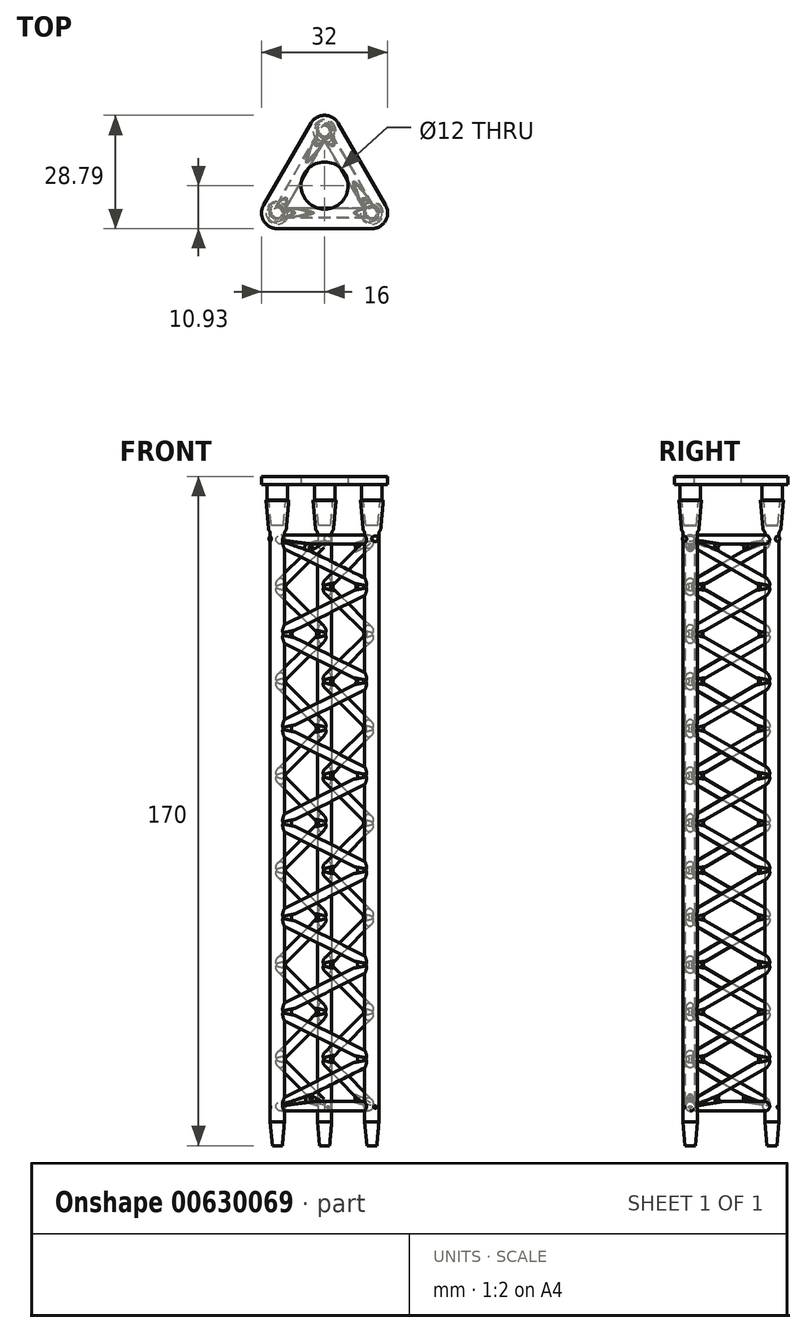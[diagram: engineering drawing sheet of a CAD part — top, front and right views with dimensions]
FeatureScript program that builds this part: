
annotation { "Feature Type Name" : "Feature", "Feature Type Description" : "" }
export const myFeature = defineFeature(function(context is Context, id is Id, definition is map)
    precondition{}
    {
        {
            var Q0;
            Q0=qCreatedBy(makeId("Top.planeOp"),FACE);
            var sketch = newSketch(context, id + "F0", { "sketchPlane" : qUnion([Q0])});
            skLineSegment(sketch, "E0", {"start": v(-12, -6.93) * mm, "end": v(12, -6.93) * mm});
            skLineSegment(sketch, "E1", {"start": v(12, -6.93) * mm, "end": v(0, 13.86) * mm});
            skLineSegment(sketch, "E2", {"start": v(0, 13.86) * mm, "end": v(-12, -6.93) * mm});
            skLineSegment(sketch, "E3", {"start": v(-6, 3.46) * mm, "end": v(12, -6.93) * mm});
            skLineSegment(sketch, "E4", {"start": v(6, 3.46) * mm, "end": v(-12, -6.93) * mm});
            skLineSegment(sketch, "E5", {"start": v(0, 13.86) * mm, "end": v(0, -6.93) * mm});
            skSolve(sketch);
        }
        {
            var Q0;
            Q0=qCreatedBy(makeId("Front.planeOp"),FACE);
            var sketch = newSketch(context, id + "F1", { "sketchPlane" : qUnion([Q0])});
            skLineSegment(sketch, "E6", {"start": v(0, 0) * mm, "end": v(0, 15.44) * mm});
            skSolve(sketch);
        }
        {
            var Q0;
            Q0=qCreatedBy(makeId("Top.planeOp"),FACE);
            var sketch = newSketch(context, id + "F2", { "sketchPlane" : qUnion([Q0])});
            skCircle(sketch, "E7", {"center": v(-12, -6.93) * mm, "radius": 1.8 * mm});
            skSolve(sketch);
        }
        {
            var Q0;
            Q0=makeQuery(id+"F2.imprint","IMPRINT",FACE,{"disambiguationData":[TD([[makeQuery(id+"F2.imprint","IMPRINT",EDGE,{"derivedFrom":sQuery(id+"F2.wireOp",EDGE,"E7")}),1.0]])]});
            var Q1;
            Q1=sQuery(id+"F2.wireOp",EDGE,"E7");
            extrude(context, id + "F3", {"entities" : qUnion([Q0]), "surfaceEntities" : qUnion([Q1]), "depth" : 154 * mm, "offsetDistance" : 25 * mm, "hasSecondDirection" : true, "secondDirectionOppositeDirection" : true, "secondDirectionDepth" : 10 * mm});
        }
        {
            var Q0;
            Q0=qCreatedBy(makeId("Right.planeOp"),FACE);
            var sketch = newSketch(context, id + "F4", { "sketchPlane" : qUnion([Q0])});
            skCircle(sketch, "E8", {"center": v(-6.93, 0) * mm, "radius": 1.2 * mm});
            skSolve(sketch);
        }
        {
            var Q0;
            Q0=sQuery(id+"F0.wireOp",EDGE,"E0");
            var Q1;
            Q1=sQuery(id+"F1.wireOp",EDGE,"E6");
            cPlane(context, id + "F5", {"entities" : qUnion([Q0, Q1]), "cplaneType" : CPlaneType.LINE_ANGLE, "offset" : 25 * mm, "angle" : 0 * degree, "width" : 150 * mm, "height" : 150 * mm});
        }
        {
            var Q0;
            Q0=qCreatedBy(id+"F5.planeOp",FACE);
            var sketch = newSketch(context, id + "F6", { "sketchPlane" : qUnion([Q0])});
            skLineSegment(sketch, "E9", {"start": v(-12, 0) * mm, "end": v(12, 12) * mm});
            skLineSegment(sketch, "E10", {"start": v(12, 12) * mm, "end": v(12, 0) * mm, "construction": true});
            skLineSegment(sketch, "E11", {"start": v(-12, 0) * mm, "end": v(-12, 24) * mm, "construction": true});
            skLineSegment(sketch, "E12", {"start": v(-12, 24) * mm, "end": v(12, 12) * mm});
            skLineSegment(sketch, "E13", {"start": v(-12, 24) * mm, "end": v(12, 36) * mm});
            skLineSegment(sketch, "E14", {"start": v(12, 36) * mm, "end": v(-12, 48) * mm});
            skLineSegment(sketch, "E15", {"start": v(-12, 48) * mm, "end": v(12, 60) * mm});
            skLineSegment(sketch, "E16", {"start": v(12, 60) * mm, "end": v(-12, 72) * mm});
            skLineSegment(sketch, "E17", {"start": v(-12, 72) * mm, "end": v(12, 84) * mm});
            skLineSegment(sketch, "E18", {"start": v(12, 84) * mm, "end": v(-12, 96) * mm});
            skLineSegment(sketch, "E19", {"start": v(-12, 96) * mm, "end": v(-12, 72) * mm, "construction": true});
            skLineSegment(sketch, "E20", {"start": v(-12, 48) * mm, "end": v(-12, 24) * mm, "construction": true});
            skLineSegment(sketch, "E21", {"start": v(-12, 48) * mm, "end": v(-12, 72) * mm, "construction": true});
            skLineSegment(sketch, "E22", {"start": v(12, 12) * mm, "end": v(12, 36) * mm, "construction": true});
            skLineSegment(sketch, "E23", {"start": v(12, 36) * mm, "end": v(12, 60) * mm, "construction": true});
            skLineSegment(sketch, "E24", {"start": v(12, 60) * mm, "end": v(12, 84) * mm, "construction": true});
            skLineSegment(sketch, "E25", {"start": v(-12, 96) * mm, "end": v(12, 108) * mm});
            skLineSegment(sketch, "E26", {"start": v(12, 108) * mm, "end": v(12, 84) * mm, "construction": true});
            skLineSegment(sketch, "E27", {"start": v(-12.25, 120) * mm, "end": v(12, 108) * mm});
            skLineSegment(sketch, "E28", {"start": v(-12.25, 120) * mm, "end": v(-12, 96) * mm, "construction": true});
            skLineSegment(sketch, "E29", {"start": v(12, 0) * mm, "end": v(-12, 0) * mm});
            skLineSegment(sketch, "E30", {"start": v(12, 108) * mm, "end": v(12, 132) * mm, "construction": true});
            skLineSegment(sketch, "E31", {"start": v(12, 132) * mm, "end": v(-12.25, 120) * mm});
            skLineSegment(sketch, "E32", {"start": v(-12.25, 120) * mm, "end": v(-12.25, 144) * mm, "construction": true});
            skLineSegment(sketch, "E33", {"start": v(12, 132) * mm, "end": v(-12.25, 144) * mm});
            skLineSegment(sketch, "E34", {"start": v(12, 144) * mm, "end": v(-12.25, 144) * mm});
            skLineSegment(sketch, "E35", {"start": v(12, 132) * mm, "end": v(12, 144) * mm, "construction": true});
            skSolve(sketch);
        }
        {
            var Q0;
            Q0=sQuery(id+"F0.wireOp",VERTEX,"E4.end");
            var Q1;
            Q1=sQuery(id+"F6.wireOp",EDGE,"E9");
            cPlane(context, id + "F7", {"entities" : qUnion([Q0, Q1]), "cplaneType" : CPlaneType.LINE_POINT, "offset" : 25 * mm, "width" : 150 * mm, "height" : 150 * mm});
        }
        {
            var Q0;
            Q0=qCreatedBy(id+"F7.planeOp",FACE);
            var sketch = newSketch(context, id + "F8", { "sketchPlane" : qUnion([Q0])});
            skCircle(sketch, "E36", {"center": v(-6.93, 5.37) * mm, "radius": 1.2 * mm});
            skSolve(sketch);
        }
        {
            var Q0;
            Q0=makeQuery(id+"F8.imprint","IMPRINT",FACE,{"disambiguationData":[TD([[makeQuery(id+"F8.imprint","IMPRINT",EDGE,{"derivedFrom":sQuery(id+"F8.wireOp",EDGE,"E36")}),1.0]])]});
            var Q1;
            Q1=sQuery(id+"F6.wireOp",EDGE,"E9");
            var Q2;
            Q2=sQuery(id+"F6.wireOp",EDGE,"E12");
            var Q3;
            Q3=sQuery(id+"F6.wireOp",EDGE,"E13");
            var Q4;
            Q4=sQuery(id+"F6.wireOp",EDGE,"E14");
            var Q5;
            Q5=sQuery(id+"F6.wireOp",EDGE,"E15");
            var Q6;
            Q6=sQuery(id+"F6.wireOp",EDGE,"E16");
            var Q7;
            Q7=sQuery(id+"F6.wireOp",EDGE,"E17");
            var Q8;
            Q8=sQuery(id+"F6.wireOp",EDGE,"E18");
            var Q9;
            Q9=sQuery(id+"F6.wireOp",EDGE,"E25");
            var Q10;
            Q10=sQuery(id+"F6.wireOp",EDGE,"E27");
            var Q11;
            Q11=sQuery(id+"F6.wireOp",EDGE,"E29");
            var Q12;
            Q12=sQuery(id+"F6.wireOp",EDGE,"E31");
            var Q13;
            Q13=sQuery(id+"F6.wireOp",EDGE,"E33");
            var Q14;
            Q14=sQuery(id+"F6.wireOp",EDGE,"E34");
            sweep(context, id + "F9", {"profiles" : qUnion([Q0]), "path" : qUnion([Q1, Q2, Q3, Q4, Q5, Q6, Q7, Q8, Q9, Q10, Q11, Q12, Q13, Q14])});
        }
        {
            var Q0;
            Q0=makeQuery(id+"F9.opSweep","MID_CAP_EDGE",EDGE,{"disambiguationData":[OSD([sQuery(id+"F6.wireOp",VERTEX,"E33.start"),sQuery(id+"F8.wireOp",EDGE,"E36")])],"capPos":12.0});
            var Q1;
            Q1=makeQuery(id+"F9.opSweep","MID_CAP_EDGE",EDGE,{"disambiguationData":[OSD([sQuery(id+"F6.wireOp",VERTEX,"E34.end"),sQuery(id+"F8.wireOp",EDGE,"E36")])],"capPos":13.0});
            var Q2;
            Q2=makeQuery(id+"F9.opSweep","MID_CAP_EDGE",EDGE,{"disambiguationData":[OSD([sQuery(id+"F6.wireOp",VERTEX,"E31.end"),sQuery(id+"F8.wireOp",EDGE,"E36")])],"capPos":11.0});
            var Q3;
            Q3=makeQuery(id+"F9.opSweep","MID_CAP_EDGE",EDGE,{"disambiguationData":[OSD([sQuery(id+"F6.wireOp",VERTEX,"E27.end"),sQuery(id+"F8.wireOp",EDGE,"E36")])],"capPos":10.0});
            var Q4;
            Q4=makeQuery(id+"F9.opSweep","MID_CAP_EDGE",EDGE,{"disambiguationData":[OSD([sQuery(id+"F6.wireOp",VERTEX,"E25.start"),sQuery(id+"F8.wireOp",EDGE,"E36")])],"capPos":9.0});
            var Q5;
            Q5=makeQuery(id+"F9.opSweep","MID_CAP_EDGE",EDGE,{"disambiguationData":[OSD([sQuery(id+"F6.wireOp",VERTEX,"E18.start"),sQuery(id+"F8.wireOp",EDGE,"E36")])],"capPos":8.0});
            var Q6;
            Q6=makeQuery(id+"F9.opSweep","MID_CAP_EDGE",EDGE,{"disambiguationData":[OSD([sQuery(id+"F6.wireOp",VERTEX,"E17.start"),sQuery(id+"F8.wireOp",EDGE,"E36")])],"capPos":7.0});
            var Q7;
            Q7=makeQuery(id+"F9.opSweep","MID_CAP_EDGE",EDGE,{"disambiguationData":[OSD([sQuery(id+"F6.wireOp",VERTEX,"E16.start"),sQuery(id+"F8.wireOp",EDGE,"E36")])],"capPos":6.0});
            var Q8;
            Q8=makeQuery(id+"F9.opSweep","MID_CAP_EDGE",EDGE,{"disambiguationData":[OSD([sQuery(id+"F6.wireOp",VERTEX,"E15.start"),sQuery(id+"F8.wireOp",EDGE,"E36")])],"capPos":5.0});
            var Q9;
            Q9=makeQuery(id+"F9.opSweep","MID_CAP_EDGE",EDGE,{"disambiguationData":[OSD([sQuery(id+"F6.wireOp",VERTEX,"E14.start"),sQuery(id+"F8.wireOp",EDGE,"E36")])],"capPos":4.0});
            var Q10;
            Q10=makeQuery(id+"F9.opSweep","MID_CAP_EDGE",EDGE,{"disambiguationData":[OSD([sQuery(id+"F6.wireOp",VERTEX,"E13.start"),sQuery(id+"F8.wireOp",EDGE,"E36")])],"capPos":3.0});
            var Q11;
            Q11=makeQuery(id+"F9.opSweep","MID_CAP_EDGE",EDGE,{"disambiguationData":[OSD([sQuery(id+"F6.wireOp",VERTEX,"E12.end"),sQuery(id+"F8.wireOp",EDGE,"E36")])],"capPos":2.0});
            var Q12;
            Q12=makeQuery(id+"F9.opSweep","MID_CAP_EDGE",EDGE,{"disambiguationData":[OSD([sQuery(id+"F6.wireOp",VERTEX,"E29.end"),sQuery(id+"F8.wireOp",EDGE,"E36")])],"capPos":1.0});
            fillet(context, id + "F10", {"entities" : qUnion([Q0, Q1, Q2, Q3, Q4, Q5, Q6, Q7, Q8, Q9, Q10, Q11, Q12]), "radius" : 1 * mm, "tangentPropagation" : true, "defaultsChanged" : false, "vertexSettings" : [], "allowEdgeOverflow" : false});
        }
        {
            var Q0;
            Q0=makeQuery(id+"FOFZZQhrRr9CB2q_1.opPattern","COPY",BODY,{"derivedFrom":makeQuery(id+"FBj1d7q4FQKIzEE_0.opExtrude","SWEPT_BODY",BODY,{"disambiguationData":[OSD([sQuery(id+"F4.wireOp",EDGE,"E8")])]}),"instanceName":"1"});
            var Q1;
            Q1=makeQuery(id+"FBj1d7q4FQKIzEE_0.opExtrude","SWEPT_BODY",BODY,{"disambiguationData":[OSD([sQuery(id+"F4.wireOp",EDGE,"E8")])]});
            var Q2;
            Q2=makeQuery(id+"F3.opExtrude","SWEPT_BODY",BODY,{"disambiguationData":[OSD([sQuery(id+"F2.wireOp",EDGE,"E7")])]});
            var Q3;
            Q3=makeQuery(id+"F9.opSweep","SWEPT_BODY",BODY,{"disambiguationData":[OSD([sQuery(id+"F6.wireOp",EDGE,"E27"),sQuery(id+"F8.wireOp",EDGE,"E36")])]});
            var Q4;
            Q4=sQuery(id+"F1.wireOp",EDGE,"E6");
            circularPattern(context, id + "F11", {"entities" : qUnion([Q0, Q1, Q2, Q3]), "axis" : qUnion([Q4]), "angle" : 360 * degree, "instanceCount" : 3, "equalSpace" : true});
        }
        {
            var Q0;
            Q0=makeQuery(id+"F9.opSweep","SWEPT_BODY",BODY,{"disambiguationData":[OSD([sQuery(id+"F6.wireOp",EDGE,"E27"),sQuery(id+"F8.wireOp",EDGE,"E36")])]});
            var Q1;
            Q1=makeQuery(id+"F11.opPattern","COPY",BODY,{"derivedFrom":makeQuery(id+"F9.opSweep","SWEPT_BODY",BODY,{"disambiguationData":[OSD([sQuery(id+"F6.wireOp",EDGE,"E27"),sQuery(id+"F8.wireOp",EDGE,"E36")])]}),"instanceName":"1"});
            var Q2;
            Q2=makeQuery(id+"F11.opPattern","COPY",BODY,{"derivedFrom":makeQuery(id+"F9.opSweep","SWEPT_BODY",BODY,{"disambiguationData":[OSD([sQuery(id+"F6.wireOp",EDGE,"E27"),sQuery(id+"F8.wireOp",EDGE,"E36")])]}),"instanceName":"2"});
            var Q3;
            Q3=makeQuery(id+"F11.opPattern","COPY",BODY,{"derivedFrom":makeQuery(id+"FOFZZQhrRr9CB2q_1.opPattern","COPY",BODY,{"derivedFrom":makeQuery(id+"FBj1d7q4FQKIzEE_0.opExtrude","SWEPT_BODY",BODY,{"disambiguationData":[OSD([sQuery(id+"F4.wireOp",EDGE,"E8")])]}),"instanceName":"1"}),"instanceName":"2"});
            var Q4;
            Q4=makeQuery(id+"F3.opExtrude","SWEPT_BODY",BODY,{"disambiguationData":[OSD([sQuery(id+"F2.wireOp",EDGE,"E7")])]});
            var Q5;
            Q5=makeQuery(id+"FBj1d7q4FQKIzEE_0.opExtrude","SWEPT_BODY",BODY,{"disambiguationData":[OSD([sQuery(id+"F4.wireOp",EDGE,"E8")])]});
            var Q6;
            Q6=makeQuery(id+"F11.opPattern","COPY",BODY,{"derivedFrom":makeQuery(id+"F3.opExtrude","SWEPT_BODY",BODY,{"disambiguationData":[OSD([sQuery(id+"F2.wireOp",EDGE,"E7")])]}),"instanceName":"1"});
            var Q7;
            Q7=makeQuery(id+"F11.opPattern","COPY",BODY,{"derivedFrom":makeQuery(id+"F3.opExtrude","SWEPT_BODY",BODY,{"disambiguationData":[OSD([sQuery(id+"F2.wireOp",EDGE,"E7")])]}),"instanceName":"2"});
            var Q8;
            Q8=makeQuery(id+"F11.opPattern","COPY",BODY,{"derivedFrom":makeQuery(id+"FBj1d7q4FQKIzEE_0.opExtrude","SWEPT_BODY",BODY,{"disambiguationData":[OSD([sQuery(id+"F4.wireOp",EDGE,"E8")])]}),"instanceName":"2"});
            var Q9;
            Q9=makeQuery(id+"F11.opPattern","COPY",BODY,{"derivedFrom":makeQuery(id+"FOFZZQhrRr9CB2q_1.opPattern","COPY",BODY,{"derivedFrom":makeQuery(id+"FBj1d7q4FQKIzEE_0.opExtrude","SWEPT_BODY",BODY,{"disambiguationData":[OSD([sQuery(id+"F4.wireOp",EDGE,"E8")])]}),"instanceName":"1"}),"instanceName":"1"});
            var Q10;
            Q10=makeQuery(id+"FOFZZQhrRr9CB2q_1.opPattern","COPY",BODY,{"derivedFrom":makeQuery(id+"FBj1d7q4FQKIzEE_0.opExtrude","SWEPT_BODY",BODY,{"disambiguationData":[OSD([sQuery(id+"F4.wireOp",EDGE,"E8")])]}),"instanceName":"1"});
            var Q11;
            Q11=makeQuery(id+"F11.opPattern","COPY",BODY,{"derivedFrom":makeQuery(id+"FBj1d7q4FQKIzEE_0.opExtrude","SWEPT_BODY",BODY,{"disambiguationData":[OSD([sQuery(id+"F4.wireOp",EDGE,"E8")])]}),"instanceName":"1"});
            booleanBodies(context, id + "F12", {"operationType" : BooleanOperationType.UNION, "tools" : qUnion([Q0, Q1, Q2, Q3, Q4, Q5, Q6, Q7, Q8, Q9, Q10, Q11])});
        }
        {
            var Q0;
            Q0=makeQuery(id+"F3.opExtrude","CAP_FACE",FACE,{"disambiguationData":[OSD([sQuery(id+"F2.wireOp",EDGE,"E7")])],"isStart":false});
            var sketch = newSketch(context, id + "F13", { "sketchPlane" : qUnion([Q0])});
            skCircle(sketch, "E37", {"center": v(-12, -6.93) * mm, "radius": 1.2 * mm});
            skCircle(sketch, "E38", {"center": v(0, 13.86) * mm, "radius": 1.2 * mm});
            skCircle(sketch, "E39", {"center": v(12, -6.93) * mm, "radius": 1.2 * mm});
            skCircle(sketch, "E40", {"center": v(0, 13.86) * mm, "radius": 2.9 * mm});
            skCircle(sketch, "E41", {"center": v(12, -6.93) * mm, "radius": 2.9 * mm});
            skCircle(sketch, "E42", {"center": v(-12, -6.93) * mm, "radius": 2.9 * mm});
            skSolve(sketch);
        }
        {
            var Q0;
            Q0=makeQuery(id+"F13.imprint","IMPRINT",FACE,{"disambiguationData":[TD([[makeQuery(id+"F13.imprint","IMPRINT",EDGE,{"derivedFrom":sQuery(id+"F13.wireOp",EDGE,"E38")}),-1.0]])]});
            var Q1;
            Q1=makeQuery(id+"F13.imprint","IMPRINT",FACE,{"disambiguationData":[TD([[makeQuery(id+"F13.imprint","IMPRINT",EDGE,{"derivedFrom":sQuery(id+"F13.wireOp",EDGE,"E39")}),-1.0]])]});
            var Q2;
            Q2=makeQuery(id+"F13.imprint","IMPRINT",FACE,{"disambiguationData":[TD([[makeQuery(id+"F13.imprint","IMPRINT",EDGE,{"derivedFrom":sQuery(id+"F13.wireOp",EDGE,"E42")}),1.0]])]});
            extrude(context, id + "F14", {"entities" : qUnion([Q0, Q1, Q2]), "operationType" : NewBodyOperationType.ADD, "oppositeDirection" : true, "depth" : 8 * mm, "offsetDistance" : 25 * mm});
        }
        {
            var Q0;
            Q0=makeQuery(id+"F14.opExtrude","CAP_EDGE",EDGE,{"disambiguationData":[OSD([sQuery(id+"F13.wireOp",EDGE,"E41")])],"isStart":false});
            var Q1;
            Q1=makeQuery(id+"F14.opExtrude","CAP_EDGE",EDGE,{"disambiguationData":[OSD([sQuery(id+"F13.wireOp",EDGE,"E40")])],"isStart":false});
            var Q2;
            Q2=makeQuery(id+"F14.opExtrude","CAP_EDGE",EDGE,{"disambiguationData":[OSD([sQuery(id+"F13.wireOp",EDGE,"E42")])],"isStart":false});
            chamfer(context, id + "F15", {"entities" : qUnion([Q0, Q1, Q2]), "chamferType" : ChamferType.OFFSET_ANGLE, "width" : 7.9 * mm, "oppositeDirection" : false, "angle" : 5 * degree, "tangentPropagation" : true});
        }
        {
            var Q0;
            Q0=makeQuery(id+"F14.boolean.opBoolean","MERGE",FACE,{"derivedFrom":[makeQuery(id+"F11.opPattern","COPY",FACE,{"derivedFrom":makeQuery(id+"F3.opExtrude","CAP_FACE",FACE,{"disambiguationData":[OSD([sQuery(id+"F2.wireOp",EDGE,"E7")])],"isStart":false}),"instanceName":"2"}),makeQuery(id+"F14.opExtrude","CAP_FACE",FACE,{"disambiguationData":[OSD([sQuery(id+"F13.wireOp",EDGE,"E38"),sQuery(id+"F13.wireOp",EDGE,"E40")])],"isStart":true})]});
            var sketch = newSketch(context, id + "F16", { "sketchPlane" : qUnion([Q0])});
            skCircle(sketch, "E43", {"center": v(0, 13.86) * mm, "radius": 2.1 * mm});
            skCircle(sketch, "E44", {"center": v(12, -6.93) * mm, "radius": 2.1 * mm});
            skCircle(sketch, "E45", {"center": v(-12, -6.93) * mm, "radius": 2.1 * mm});
            skSolve(sketch);
        }
        {
            var Q0;
            Q0=makeQuery(id+"F16.imprint","IMPRINT",FACE,{"disambiguationData":[TD([[makeQuery(id+"F16.imprint","IMPRINT",EDGE,{"derivedFrom":sQuery(id+"F16.wireOp",EDGE,"E43")}),1.0]])]});
            var Q1;
            Q1=makeQuery(id+"F16.imprint","IMPRINT",FACE,{"disambiguationData":[TD([[makeQuery(id+"F16.imprint","IMPRINT",EDGE,{"derivedFrom":sQuery(id+"F16.wireOp",EDGE,"E44")}),1.0]])]});
            var Q2;
            Q2=makeQuery(id+"F16.imprint","IMPRINT",FACE,{"disambiguationData":[TD([[makeQuery(id+"F16.imprint","IMPRINT",EDGE,{"derivedFrom":sQuery(id+"F16.wireOp",EDGE,"E45")}),1.0]])]});
            extrude(context, id + "F17", {"entities" : qUnion([Q0, Q1, Q2]), "operationType" : NewBodyOperationType.REMOVE, "oppositeDirection" : true, "depth" : 6.5 * mm, "offsetDistance" : 25 * mm, "hasDraft" : true, "draftAngle" : 5 * degree, "draftPullDirection" : true});
        }
        {
            var Q0;
            Q0=makeQuery(id+"F3.opExtrude","CAP_EDGE",EDGE,{"disambiguationData":[OSD([sQuery(id+"F2.wireOp",EDGE,"E7")])],"isStart":true});
            var Q1;
            Q1=makeQuery(id+"F11.opPattern","COPY",EDGE,{"derivedFrom":makeQuery(id+"F3.opExtrude","CAP_EDGE",EDGE,{"disambiguationData":[OSD([sQuery(id+"F2.wireOp",EDGE,"E7")])],"isStart":true}),"instanceName":"1"});
            var Q2;
            Q2=makeQuery(id+"F11.opPattern","COPY",EDGE,{"derivedFrom":makeQuery(id+"F3.opExtrude","CAP_EDGE",EDGE,{"disambiguationData":[OSD([sQuery(id+"F2.wireOp",EDGE,"E7")])],"isStart":true}),"instanceName":"2"});
            chamfer(context, id + "F18", {"entities" : qUnion([Q0, Q1, Q2]), "chamferType" : ChamferType.OFFSET_ANGLE, "width" : 6 * mm, "oppositeDirection" : false, "angle" : 5 * degree, "tangentPropagation" : true});
        }
        {
            var Q0;
            Q0=makeQuery(id+"F14.boolean.opBoolean","MERGE",FACE,{"derivedFrom":[makeQuery(id+"F11.opPattern","COPY",FACE,{"derivedFrom":makeQuery(id+"F3.opExtrude","CAP_FACE",FACE,{"disambiguationData":[OSD([sQuery(id+"F2.wireOp",EDGE,"E7")])],"isStart":false}),"instanceName":"1"}),makeQuery(id+"F14.opExtrude","CAP_FACE",FACE,{"disambiguationData":[OSD([sQuery(id+"F13.wireOp",EDGE,"E39"),sQuery(id+"F13.wireOp",EDGE,"E41")])],"isStart":true})]});
            var sketch = newSketch(context, id + "F19", { "sketchPlane" : qUnion([Q0])});
            skCircle(sketch, "E46", {"center": v(0, 13.86) * mm, "radius": 2.6 * mm});
            skCircle(sketch, "E47", {"center": v(12, -6.93) * mm, "radius": 2.6 * mm});
            skCircle(sketch, "E48", {"center": v(-12, -6.93) * mm, "radius": 2.6 * mm});
            skSolve(sketch);
        }
        {
            var Q0;
            Q0=makeQuery(id+"F19.imprint","IMPRINT",FACE,{"disambiguationData":[TD([[makeQuery(id+"F19.imprint","IMPRINT",EDGE,{"derivedFrom":sQuery(id+"F19.wireOp",EDGE,"E48")}),1.0]])]});
            var Q1;
            Q1=makeQuery(id+"F19.imprint","IMPRINT",FACE,{"disambiguationData":[TD([[makeQuery(id+"F19.imprint","IMPRINT",EDGE,{"derivedFrom":sQuery(id+"F19.wireOp",EDGE,"E47")}),1.0]])]});
            var Q2;
            Q2=makeQuery(id+"F19.imprint","IMPRINT",FACE,{"disambiguationData":[TD([[makeQuery(id+"F19.imprint","IMPRINT",EDGE,{"derivedFrom":sQuery(id+"F19.wireOp",EDGE,"E46")}),1.0]])]});
            var Q3;
            Q3=makeQuery(id+"F16.imprint","IMPRINT",FACE,{"disambiguationData":[TD([[makeQuery(id+"F16.imprint","IMPRINT",EDGE,{"derivedFrom":sQuery(id+"F16.wireOp",EDGE,"E44")}),1.0]])]});
            extrude(context, id + "F20", {"entities" : qUnion([Q0, Q1, Q2, Q3]), "operationType" : NewBodyOperationType.ADD, "depth" : 4 * mm, "offsetDistance" : 25 * mm});
        }
        {
            var Q0;
            Q0=makeQuery(id+"F20.opExtrude","CAP_FACE",FACE,{"disambiguationData":[OSD([sQuery(id+"F19.wireOp",EDGE,"E48")])],"isStart":false});
            var sketch = newSketch(context, id + "F21", { "sketchPlane" : qUnion([Q0])});
            skCircle(sketch, "E49", {"center": v(-12, -6.93) * mm, "radius": 4 * mm});
            skCircle(sketch, "E50", {"center": v(0, 13.86) * mm, "radius": 4 * mm});
            skCircle(sketch, "E51", {"center": v(12, -6.93) * mm, "radius": 4 * mm});
            skLineSegment(sketch, "E52", {"start": v(-15.46, -4.93) * mm, "end": v(-3.46, 15.86) * mm});
            skLineSegment(sketch, "E53", {"start": v(-12, -10.93) * mm, "end": v(12, -10.93) * mm});
            skLineSegment(sketch, "E54", {"start": v(3.46, 15.86) * mm, "end": v(15.46, -4.93) * mm});
            skLineSegment(sketch, "E55", {"start": v(-9.46, 5.46) * mm, "end": v(0, 0) * mm, "construction": true});
            skLineSegment(sketch, "E56", {"start": v(0, 0) * mm, "end": v(9.46, 5.46) * mm, "construction": true});
            skLineSegment(sketch, "E57", {"start": v(0, 0) * mm, "end": v(0, -10.93) * mm, "construction": true});
            skCircle(sketch, "E58", {"center": v(0, 0) * mm, "radius": 6 * mm});
            skSolve(sketch);
        }
        {
            var Q0;
            {var subQ0=sQuery(id+"F21.wireOp",EDGE,"E51");var subQ1=makeQuery(id+"F21.imprint","INTERSECT",VERTEX,{"derivedFrom":[subQ0,sQuery(id+"F21.wireOp",EDGE,"E53")]});Q0=makeQuery(id+"F21.imprint","IMPRINT",FACE,{"disambiguationData":[TD([[makeQuery(id+"F21.imprint","IMPRINT",EDGE,{"disambiguationData":[TD([[subQ1,1.0]])],"derivedFrom":subQ0}),1.0]])]});}
            var Q1;
            {var subQ3=sQuery(id+"F21.wireOp",EDGE,"E52");Q1=makeQuery(id+"F21.imprint","IMPRINT",FACE,{"disambiguationData":[TD([[makeQuery(id+"F21.imprint","IMPRINT",EDGE,{"derivedFrom":subQ3}),-1.0]])]});}
            var Q2;
            Q2=makeQuery(id+"F21.imprint","IMPRINT",FACE,{"disambiguationData":[TD([[makeQuery(id+"F21.imprint","IMPRINT",EDGE,{"derivedFrom":makeQuery(id+"F20.opExtrude","CAP_EDGE",EDGE,{"disambiguationData":[OSD([sQuery(id+"F19.wireOp",EDGE,"E48")])],"isStart":false})}),-1.0]])]});
            var Q3;
            Q3=makeQuery(id+"F21.imprint","IMPRINT",FACE,{"disambiguationData":[TD([[makeQuery(id+"F21.imprint","IMPRINT",EDGE,{"derivedFrom":makeQuery(id+"F20.opExtrude","CAP_EDGE",EDGE,{"disambiguationData":[OSD([sQuery(id+"F19.wireOp",EDGE,"E48")])],"isStart":false})}),1.0]])]});
            var Q4;
            {var subQ0=sQuery(id+"F21.wireOp",EDGE,"E50");var subQ1=makeQuery(id+"F21.imprint","INTERSECT",VERTEX,{"derivedFrom":[subQ0,sQuery(id+"F21.wireOp",EDGE,"E52")]});Q4=makeQuery(id+"F21.imprint","IMPRINT",FACE,{"disambiguationData":[TD([[makeQuery(id+"F21.imprint","IMPRINT",EDGE,{"disambiguationData":[TD([[subQ1,1.0]])],"derivedFrom":subQ0}),1.0]])]});}
            extrude(context, id + "F22", {"entities" : qUnion([Q0, Q1, Q2, Q3, Q4]), "operationType" : NewBodyOperationType.ADD, "depth" : 2 * mm, "offsetDistance" : 25 * mm});
        }
        {
            var Q0;
            {var subQ0=sQuery(id+"F13.wireOp",EDGE,"E41");Q0=makeQuery(id+"F15.opChamfer","BLEND_EDGE",EDGE,{"blendedFrom":[makeQuery(id+"F14.opExtrude","CAP_EDGE",EDGE,{"disambiguationData":[OSD([subQ0])],"isStart":false}),makeQuery(id+"F14.opExtrude","CAP_FACE",FACE,{"disambiguationData":[OSD([sQuery(id+"F13.wireOp",EDGE,"E39"),subQ0])],"isStart":false})],"blendedInto":[makeQuery(id+"F14.opExtrude","CAP_FACE",FACE,{"disambiguationData":[OSD([sQuery(id+"F13.wireOp",EDGE,"E39"),subQ0])],"isStart":false})]});}
            var Q1;
            {var subQ0=sQuery(id+"F13.wireOp",EDGE,"E42");Q1=makeQuery(id+"F15.opChamfer","BLEND_EDGE",EDGE,{"blendedFrom":[makeQuery(id+"F14.opExtrude","CAP_EDGE",EDGE,{"disambiguationData":[OSD([subQ0])],"isStart":false}),makeQuery(id+"F14.opExtrude","CAP_FACE",FACE,{"disambiguationData":[OSD([sQuery(id+"F2.wireOp",EDGE,"E7"),subQ0])],"isStart":false})],"blendedInto":[makeQuery(id+"F14.opExtrude","CAP_FACE",FACE,{"disambiguationData":[OSD([sQuery(id+"F2.wireOp",EDGE,"E7"),subQ0])],"isStart":false})]});}
            var Q2;
            {var subQ0=sQuery(id+"F13.wireOp",EDGE,"E40");Q2=makeQuery(id+"F15.opChamfer","BLEND_EDGE",EDGE,{"blendedFrom":[makeQuery(id+"F14.opExtrude","CAP_EDGE",EDGE,{"disambiguationData":[OSD([subQ0])],"isStart":false}),makeQuery(id+"F14.opExtrude","CAP_FACE",FACE,{"disambiguationData":[OSD([sQuery(id+"F13.wireOp",EDGE,"E38"),subQ0])],"isStart":false})],"blendedInto":[makeQuery(id+"F14.opExtrude","CAP_FACE",FACE,{"disambiguationData":[OSD([sQuery(id+"F13.wireOp",EDGE,"E38"),subQ0])],"isStart":false})]});}
            fillet(context, id + "F23", {"entities" : qUnion([Q0, Q1, Q2]), "radius" : 1 * mm, "tangentPropagation" : true, "allowEdgeOverflow" : false});
        }
        {
            var Q0;
            {var subQ2=sQuery(id+"F2.wireOp",EDGE,"E7");var subQ3=makeQuery(id+"F11.opPattern","COPY",FACE,{"derivedFrom":makeQuery(id+"F3.opExtrude","SWEPT_FACE",FACE,{"disambiguationData":[OSD([subQ2])]}),"instanceName":"2"});var subQ49=sQuery(id+"F13.wireOp",EDGE,"E40");var subQ50=makeQuery(id+"F14.opExtrude","CAP_FACE",FACE,{"disambiguationData":[OSD([sQuery(id+"F13.wireOp",EDGE,"E38"),subQ49])],"isStart":false});Q0=makeQuery(id+"F23.opFillet","BLEND_EDGE",EDGE,{"blendedFrom":[makeQuery(id+"F15.opChamfer","BLEND_EDGE",EDGE,{"blendedFrom":[makeQuery(id+"F14.opExtrude","CAP_EDGE",EDGE,{"disambiguationData":[OSD([subQ49])],"isStart":false}),subQ50],"blendedInto":[subQ50]}),makeQuery(id+"F14.boolean.opBoolean","SPLIT",FACE,{"disambiguationData":[TD([makeQuery(id+"F11.opPattern","COPY",FACE,{"derivedFrom":makeQuery(id+"F3.opExtrude","CAP_FACE",FACE,{"disambiguationData":[OSD([subQ2])],"isStart":true}),"instanceName":"2"})])],"derivedFrom":subQ3})],"blendedInto":[makeQuery(id+"F14.boolean.opBoolean","SPLIT",FACE,{"disambiguationData":[TD([makeQuery(id+"F11.opPattern","COPY",FACE,{"derivedFrom":makeQuery(id+"F3.opExtrude","CAP_FACE",FACE,{"disambiguationData":[OSD([subQ2])],"isStart":true}),"instanceName":"2"})])],"derivedFrom":subQ3})]});}
            var Q1;
            {var subQ2=sQuery(id+"F2.wireOp",EDGE,"E7");var subQ3=makeQuery(id+"F3.opExtrude","SWEPT_FACE",FACE,{"disambiguationData":[OSD([subQ2])]});var subQ41=sQuery(id+"F13.wireOp",EDGE,"E42");var subQ42=makeQuery(id+"F14.opExtrude","CAP_FACE",FACE,{"disambiguationData":[OSD([subQ2,subQ41])],"isStart":false});Q1=makeQuery(id+"F23.opFillet","BLEND_EDGE",EDGE,{"blendedFrom":[makeQuery(id+"F15.opChamfer","BLEND_EDGE",EDGE,{"blendedFrom":[makeQuery(id+"F14.opExtrude","CAP_EDGE",EDGE,{"disambiguationData":[OSD([subQ41])],"isStart":false}),subQ42],"blendedInto":[subQ42]}),makeQuery(id+"F14.boolean.opBoolean","SPLIT",FACE,{"disambiguationData":[TD([makeQuery(id+"F3.opExtrude","CAP_FACE",FACE,{"disambiguationData":[OSD([subQ2])],"isStart":true})])],"derivedFrom":subQ3})],"blendedInto":[makeQuery(id+"F14.boolean.opBoolean","SPLIT",FACE,{"disambiguationData":[TD([makeQuery(id+"F3.opExtrude","CAP_FACE",FACE,{"disambiguationData":[OSD([subQ2])],"isStart":true})])],"derivedFrom":subQ3})]});}
            var Q2;
            {var subQ4=sQuery(id+"F2.wireOp",EDGE,"E7");var subQ5=makeQuery(id+"F11.opPattern","COPY",FACE,{"derivedFrom":makeQuery(id+"F3.opExtrude","SWEPT_FACE",FACE,{"disambiguationData":[OSD([subQ4])]}),"instanceName":"1"});var subQ43=sQuery(id+"F13.wireOp",EDGE,"E41");var subQ44=makeQuery(id+"F14.opExtrude","CAP_FACE",FACE,{"disambiguationData":[OSD([sQuery(id+"F13.wireOp",EDGE,"E39"),subQ43])],"isStart":false});Q2=makeQuery(id+"F23.opFillet","BLEND_EDGE",EDGE,{"blendedFrom":[makeQuery(id+"F15.opChamfer","BLEND_EDGE",EDGE,{"blendedFrom":[makeQuery(id+"F14.opExtrude","CAP_EDGE",EDGE,{"disambiguationData":[OSD([subQ43])],"isStart":false}),subQ44],"blendedInto":[subQ44]}),makeQuery(id+"F14.boolean.opBoolean","SPLIT",FACE,{"disambiguationData":[TD([makeQuery(id+"F11.opPattern","COPY",FACE,{"derivedFrom":makeQuery(id+"F3.opExtrude","CAP_FACE",FACE,{"disambiguationData":[OSD([subQ4])],"isStart":true}),"instanceName":"1"})])],"derivedFrom":subQ5})],"blendedInto":[makeQuery(id+"F14.boolean.opBoolean","SPLIT",FACE,{"disambiguationData":[TD([makeQuery(id+"F11.opPattern","COPY",FACE,{"derivedFrom":makeQuery(id+"F3.opExtrude","CAP_FACE",FACE,{"disambiguationData":[OSD([subQ4])],"isStart":true}),"instanceName":"1"})])],"derivedFrom":subQ5})]});}
            fillet(context, id + "F24", {"entities" : qUnion([Q0, Q1, Q2]), "radius" : 1 * mm, "tangentPropagation" : true, "allowEdgeOverflow" : false});
        }
    });
